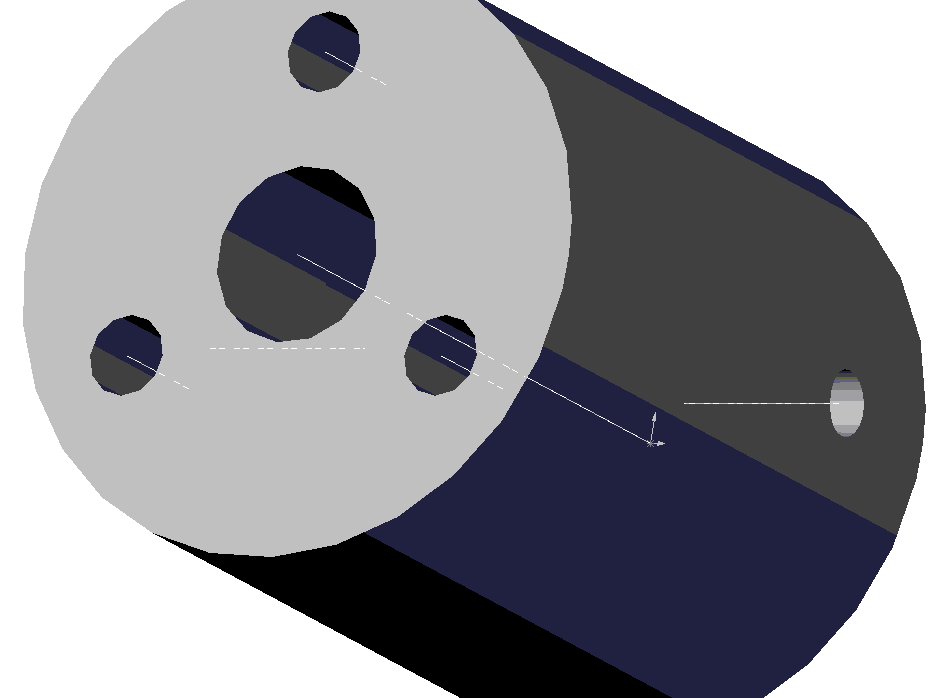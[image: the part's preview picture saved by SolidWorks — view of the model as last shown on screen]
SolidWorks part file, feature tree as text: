
SOLIDWORKS PART (.sldprt)
format: sldprt  version: not decoded by parser v0  size: 151,552 bytes
history: native  units: mm
features: sketch x6, cut_extrude x5, plane x3, extrude x1, pattern_circular x1 (+5 scaffold rows collapsed)
feature tree (21):
  scaffold x5  (default folders/planes/origin — collapsed)
  plane  "Plane1"
  plane  "Plane2"
  plane  "Plane3"
  sketch  "Sketch1"  dims[D1=30.0mm D2=30.0mm]
  extrude  "Base-Extrude"  Depth=35mm
  sketch  "Sketch2"  dims[D1=12.0mm D2=30.0mm]
  cut_extrude  "Cut-Extrude1"  Depth=25mm
  sketch  "Sketch3"  dims[D1=8.75mm]
  cut_extrude  "Cut-Extrude2"  Depth=25mm
  sketch  "Sketch4"  dims[D1=3.25mm D2=17.5mm D3=15.0mm]
  cut_extrude  "Cut-Extrude3"  [1 undecoded]
  sketch  "Sketch5"  dims[D1=3.25mm D2=7.5mm D3=15.0mm]
  cut_extrude  "Cut-Extrude4"  [1 undecoded]
  sketch  "Sketch6"  dims[D1=4.0mm D2=10.0mm]
  cut_extrude  "Cut-Extrude5"  Depth=7mm
  pattern_circular  "CirPattern1"  Count=3 Angle=360deg
decode coverage: 11 of 13 modeling features carry decoded parameters
note: 2 parameter values undecoded
note: suppression state not decoded; provenance and decode notes live in map.json
